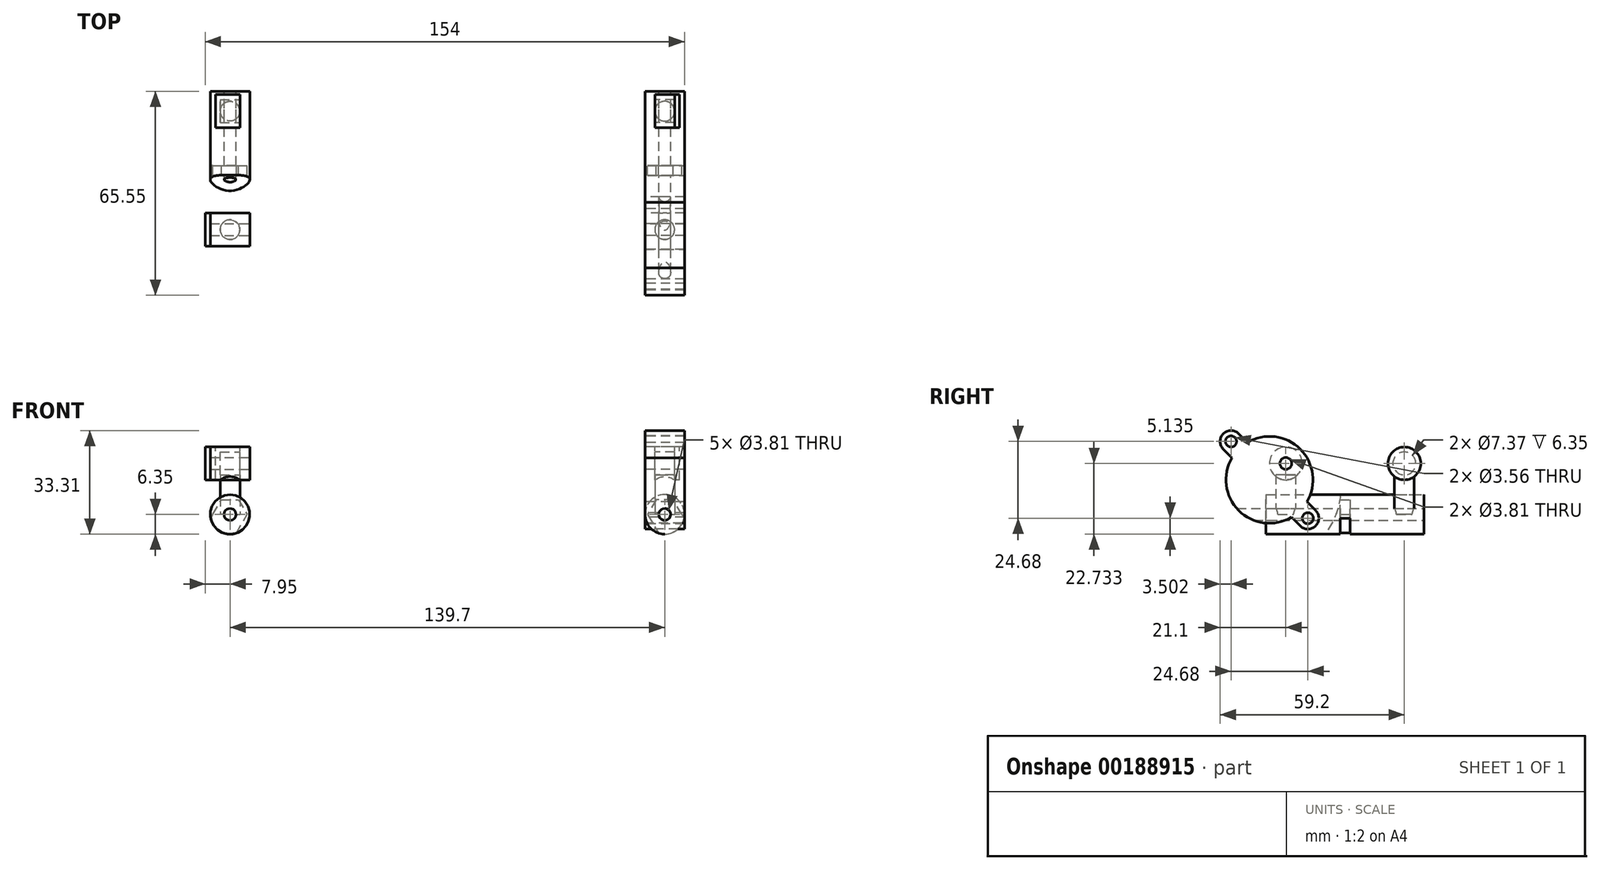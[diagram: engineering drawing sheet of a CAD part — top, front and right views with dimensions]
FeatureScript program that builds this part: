
annotation { "Feature Type Name" : "Feature", "Feature Type Description" : "" }
export const myFeature = defineFeature(function(context is Context, id is Id, definition is map)
    precondition{}
    {
        {
            var Q0;
            Q0=qCreatedBy(makeId("Front.planeOp"),FACE);
            var sketch = newSketch(context, id + "F0", { "sketchPlane" : qUnion([Q0])});
            skCircle(sketch, "E0", {"center": v(-69.85, 0) * mm, "radius": 1.9 * mm});
            skCircle(sketch, "E1", {"center": v(69.85, 0) * mm, "radius": 1.9 * mm});
            skLineSegment(sketch, "E2", {"start": v(-69.85, 0) * mm, "end": v(0, 0) * mm, "construction": true});
            skLineSegment(sketch, "E3", {"start": v(69.85, 0) * mm, "end": v(0, 0) * mm, "construction": true});
            skArc(sketch, "E4", {"start": v(-69.85, 6.35) * mm, "mid": v(-74.34, -4.5) * mm, "end": v(-63.5, 0) * mm});
            skArc(sketch, "E5", {"start": v(63.5, 0) * mm, "mid": v(74.34, -4.5) * mm, "end": v(69.85, 6.35) * mm});
            skLineSegment(sketch, "E6", {"start": v(69.85, 6.35) * mm, "end": v(69.85, 0) * mm, "construction": true});
            skLineSegment(sketch, "E7", {"start": v(-69.85, 6.35) * mm, "end": v(-69.85, 0) * mm, "construction": true});
            skArc(sketch, "E8", {"start": v(-63.5, 0) * mm, "mid": v(-65.36, 4.5) * mm, "end": v(-69.85, 6.35) * mm});
            skArc(sketch, "E9", {"start": v(69.85, 6.35) * mm, "mid": v(65.36, 4.5) * mm, "end": v(63.5, 0) * mm});
            skSolve(sketch);
        }
        {
            var Q0;
            Q0=qSketchRegion(id+"F0",true);
            extrude(context, id + "F1", {"entities" : qUnion([Q0]), "endBound" : BoundingType.SYMMETRIC, "depth" : 12.7 * mm});
        }
        {
            var Q0;
            Q0=makeQuery(id+"F1.opExtrude","CAP_FACE",FACE,{"disambiguationData":[OSD([sQuery(id+"F0.wireOp",EDGE,"E0"),sQuery(id+"F0.wireOp",EDGE,"E1"),sQuery(id+"F0.wireOp",EDGE,"E4"),sQuery(id+"F0.wireOp",EDGE,"E5"),sQuery(id+"F0.wireOp",EDGE,"xyxUVOh0-Lu6m-2nq8-UmFe-XEndblqHEdPT"),sQuery(id+"F0.wireOp",EDGE,"R0XNFQHJ-87U4-ma3Q-qhns-AWXhGPeFOJpI"),sQuery(id+"F0.wireOp",EDGE,"e34iIN8D-vhv8-jKHx-9azW-8f77yfFPg5bW"),sQuery(id+"F0.wireOp",EDGE,"8HNf8llB-7DT9-wTKg-WSqf-SX1znclEPI6e"),sQuery(id+"F0.wireOp",EDGE,"dpBhEA3d-197v-VctA-TAhr-BlY7lmP6uD7G"),sQuery(id+"F0.wireOp",EDGE,"sEkqqTot-DNnZ-R70t-ELHf-v8sBDht2CAfZ")])],"isStart":false});
            var sketch = newSketch(context, id + "F2", { "sketchPlane" : qUnion([Q0])});
            skCircle(sketch, "E10.0", {"center": v(-69.85, 0) * mm, "radius": 1.9 * mm});
            skLineSegment(sketch, "E10.1", {"start": v(-64.48, 3.39) * mm, "end": v(-64.48, 3.39) * mm});
            skLineSegment(sketch, "E11.MirrorCS", {"start": v(64.48, 3.39) * mm, "end": v(64.48, 3.39) * mm});
            skCircle(sketch, "E12.MirrorC", {"center": v(69.85, 0) * mm, "radius": 1.9 * mm});
            skCircle(sketch, "E13.0", {"center": v(69.85, 0) * mm, "radius": 6.35 * mm});
            skCircle(sketch, "E13.1", {"center": v(-69.85, 0) * mm, "radius": 6.35 * mm});
            skSolve(sketch);
        }
        {
            var Q0;
            Q0=qSketchRegion(id+"F2",true);
            extrude(context, id + "F3", {"entities" : qUnion([Q0]), "operationType" : NewBodyOperationType.ADD, "depth" : 19.05 * mm});
        }
        {
            var Q0;
            Q0=makeQuery(id+"F1.opExtrude","SWEPT_BODY",BODY,{"disambiguationData":[OSD([sQuery(id+"F0.wireOp",EDGE,"E0"),sQuery(id+"F0.wireOp",EDGE,"E1"),sQuery(id+"F0.wireOp",EDGE,"E4"),sQuery(id+"F0.wireOp",EDGE,"E5"),sQuery(id+"F0.wireOp",EDGE,"xyxUVOh0-Lu6m-2nq8-UmFe-XEndblqHEdPT"),sQuery(id+"F0.wireOp",EDGE,"R0XNFQHJ-87U4-ma3Q-qhns-AWXhGPeFOJpI"),sQuery(id+"F0.wireOp",EDGE,"e34iIN8D-vhv8-jKHx-9azW-8f77yfFPg5bW"),sQuery(id+"F0.wireOp",EDGE,"8HNf8llB-7DT9-wTKg-WSqf-SX1znclEPI6e"),sQuery(id+"F0.wireOp",EDGE,"dpBhEA3d-197v-VctA-TAhr-BlY7lmP6uD7G"),sQuery(id+"F0.wireOp",EDGE,"sEkqqTot-DNnZ-R70t-ELHf-v8sBDht2CAfZ")])]});
            var Q1;
            Q1=qCreatedBy(makeId("Front.planeOp"),FACE);
            mirror(context, id + "F4", {"operationType" : NewBodyOperationType.ADD, "entities" : qUnion([Q0]), "mirrorPlane" : qUnion([Q1])});
        }
        {
            var Q0;
            Q0=qCreatedBy(makeId("Front.planeOp"),FACE);
            var sketch = newSketch(context, id + "F5", { "sketchPlane" : qUnion([Q0])});
            skCircle(sketch, "E14.cCircle", {"center": v(-69.85, 0) * mm, "radius": 4.76 * mm, "construction": true});
            skLineSegment(sketch, "E14.0", {"start": v(-72.6, 4.76) * mm, "end": v(-67.1, 4.76) * mm});
            skLineSegment(sketch, "E14.1", {"start": v(-67.1, 4.76) * mm, "end": v(-64.35, 0) * mm});
            skLineSegment(sketch, "E14.2", {"start": v(-64.35, 0) * mm, "end": v(-67.1, -4.76) * mm});
            skLineSegment(sketch, "E14.5", {"start": v(-75.35, 0) * mm, "end": v(-72.6, 4.76) * mm});
            skPoint(sketch, "E14.0.midPoint", {"position": v(-69.85, 4.76) * mm});
            skLineSegment(sketch, "E15.MirrorCS", {"start": v(64.35, 0) * mm, "end": v(67.1, -4.76) * mm});
            skLineSegment(sketch, "E16.MirrorCS", {"start": v(75.35, 0) * mm, "end": v(72.6, 4.76) * mm});
            skLineSegment(sketch, "E17.MirrorCS", {"start": v(67.1, 4.76) * mm, "end": v(64.35, 0) * mm});
            skLineSegment(sketch, "E18.MirrorCS", {"start": v(72.6, 4.76) * mm, "end": v(67.1, 4.76) * mm});
            skCircle(sketch, "E19.MirrorC", {"center": v(69.85, 0) * mm, "radius": 4.76 * mm, "construction": true});
            skLineSegment(sketch, "E20", {"start": v(-75.35, 0) * mm, "end": v(-79.15, -6.2) * mm});
            skLineSegment(sketch, "E21", {"start": v(-79.15, -6.2) * mm, "end": v(-70.74, -11.07) * mm});
            skLineSegment(sketch, "E22", {"start": v(-70.74, -11.07) * mm, "end": v(-64.35, 0) * mm});
            skPoint(sketch, "E23.orphan", {"position": v(-72.6, -4.76) * mm});
            skLineSegment(sketch, "E24.MirrorCS", {"start": v(70.74, -11.07) * mm, "end": v(64.35, 0) * mm});
            skLineSegment(sketch, "E25.MirrorCS", {"start": v(75.35, 0) * mm, "end": v(79.15, -6.2) * mm});
            skLineSegment(sketch, "E26.MirrorCS", {"start": v(79.15, -6.2) * mm, "end": v(70.74, -11.07) * mm});
            skPoint(sketch, "E27.orphan", {"position": v(72.6, -4.76) * mm});
            skSolve(sketch);
        }
        {
            var Q0;
            Q0=qSketchRegion(id+"F5",true);
            extrude(context, id + "F6", {"entities" : qUnion([Q0]), "operationType" : NewBodyOperationType.REMOVE, "endBound" : BoundingType.SYMMETRIC, "depth" : 3.17 * mm});
        }
        {
            var Q0;
            Q0=qCreatedBy(makeId("Top.planeOp"),FACE);
            var sketch = newSketch(context, id + "F7", { "sketchPlane" : qUnion([Q0])});
            skCircle(sketch, "E28", {"center": v(-69.85, 19.05) * mm, "radius": 3.18 * mm});
            skCircle(sketch, "E29.MirrorC", {"center": v(69.85, 19.05) * mm, "radius": 3.18 * mm});
            skCircle(sketch, "E30", {"center": v(-69.85, -19.05) * mm, "radius": 3.18 * mm});
            skLineSegment(sketch, "E31", {"start": v(-69.85, 19.05) * mm, "end": v(-69.85, -19.05) * mm, "construction": true});
            skCircle(sketch, "E32.MirrorC", {"center": v(69.85, -19.05) * mm, "radius": 3.18 * mm});
            skSolve(sketch);
        }
        {
            var Q0;
            Q0=qSketchRegion(id+"F7",true);
            extrude(context, id + "F8", {"entities" : qUnion([Q0]), "depth" : 12.7 * mm});
        }
        {
            var Q0;
            Q0=makeQuery(id+"F4.opPattern","COPY",FACE,{"derivedFrom":makeQuery(id+"F3.opExtrude","CAP_FACE",FACE,{"disambiguationData":[OSD([sQuery(id+"F2.wireOp",EDGE,"E10.0"),sQuery(id+"F2.wireOp",EDGE,"E13.1")])],"isStart":false}),"instanceName":"1"});
            var sketch = newSketch(context, id + "F9", { "sketchPlane" : qUnion([Q0])});
            skCircle(sketch, "E33.0", {"center": v(69.85, 0) * mm, "radius": 1.9 * mm});
            skCircle(sketch, "E34.0", {"center": v(-69.85, 0) * mm, "radius": 1.9 * mm});
            skSolve(sketch);
        }
        {
            var Q0;
            Q0=qSketchRegion(id+"F9",true);
            extrude(context, id + "F10", {"entities" : qUnion([Q0]), "operationType" : NewBodyOperationType.REMOVE, "oppositeDirection" : true, "depth" : 42.23 * mm});
        }
        {
            var Q0;
            Q0=qCreatedBy(makeId("Right.planeOp"),FACE);
            cPlane(context, id + "F11", {"entities" : qUnion([Q0]), "cplaneType" : CPlaneType.OFFSET, "offset" : 69.85 * mm, "width" : 152.4 * mm, "height" : 152.4 * mm});
        }
        {
            var Q0;
            Q0=qCreatedBy(id+"F11.planeOp",FACE);
            var sketch = newSketch(context, id + "F12", { "sketchPlane" : qUnion([Q0])});
            skCircle(sketch, "E35", {"center": v(19.05, 16.38) * mm, "radius": 5.28 * mm});
            skCircle(sketch, "E36", {"center": v(19.05, 16.38) * mm, "radius": 3.68 * mm});
            skSolve(sketch);
        }
        {
            var Q0;
            Q0=qSketchRegion(id+"F12",true);
            extrude(context, id + "F13", {"entities" : qUnion([Q0]), "endBound" : BoundingType.SYMMETRIC, "depth" : 6.35 * mm});
        }
        {
            var Q0;
            Q0=makeQuery(id+"F13.opExtrude","SWEPT_BODY",BODY,{"disambiguationData":[OSD([sQuery(id+"F12.wireOp",EDGE,"E35"),sQuery(id+"F12.wireOp",EDGE,"E36")])]});
            var Q1;
            Q1=qCreatedBy(makeId("Right.planeOp"),FACE);
            mirror(context, id + "F14", {"operationType" : NewBodyOperationType.ADD, "entities" : qUnion([Q0]), "mirrorPlane" : qUnion([Q1])});
        }
        {
            var Q0;
            Q0=makeQuery(id+"F13.opExtrude","CAP_FACE",FACE,{"disambiguationData":[OSD([sQuery(id+"F12.wireOp",EDGE,"E35"),sQuery(id+"F12.wireOp",EDGE,"E36")])],"isStart":false});
            var sketch = newSketch(context, id + "F15", { "sketchPlane" : qUnion([Q0])});
            skCircle(sketch, "E37.0", {"center": v(19.05, 16.38) * mm, "radius": 5.28 * mm});
            skSolve(sketch);
        }
        {
            var Q0;
            Q0=qSketchRegion(id+"F15",true);
            extrude(context, id + "F16", {"entities" : qUnion([Q0]), "depth" : 1.52 * mm});
        }
        {
            var Q0;
            Q0=makeQuery(id+"F14.opPattern","COPY",FACE,{"derivedFrom":makeQuery(id+"F13.opExtrude","CAP_FACE",FACE,{"disambiguationData":[OSD([sQuery(id+"F12.wireOp",EDGE,"E35"),sQuery(id+"F12.wireOp",EDGE,"E36")])],"isStart":false}),"instanceName":"1"});
            var sketch = newSketch(context, id + "F17", { "sketchPlane" : qUnion([Q0])});
            skCircle(sketch, "E38.0", {"center": v(-19.05, 16.38) * mm, "radius": 5.28 * mm});
            skSolve(sketch);
        }
        {
            var Q0;
            Q0=qSketchRegion(id+"F17",true);
            extrude(context, id + "F18", {"entities" : qUnion([Q0]), "operationType" : NewBodyOperationType.ADD, "depth" : 1.52 * mm});
        }
        {
            var Q0;
            Q0=qCreatedBy(id+"F11.planeOp",FACE);
            var sketch = newSketch(context, id + "F19", { "sketchPlane" : qUnion([Q0])});
            skCircle(sketch, "E39", {"center": v(-19.05, 16.38) * mm, "radius": 1.9 * mm});
            skLineSegment(sketch, "E40", {"start": v(13.77, 16.38) * mm, "end": v(-19.05, 16.38) * mm, "construction": true});
            skCircle(sketch, "E41.0", {"center": v(19.05, 16.38) * mm, "radius": 5.28 * mm, "construction": true});
            skLineSegment(sketch, "E42", {"start": v(19.05, 16.38) * mm, "end": v(13.77, 16.38) * mm, "construction": true});
            skArc(sketch, "E43", {"start": v(-36.35, 18.21) * mm, "mid": v(-34.19, 1.25) * mm, "end": v(-17.22, -0.91) * mm});
            skArc(sketch, "E44", {"start": v(-34.17, 25.94) * mm, "mid": v(-39.12, 25.94) * mm, "end": v(-39.12, 20.99) * mm});
            skArc(sketch, "E45", {"start": v(-14.44, -3.69) * mm, "mid": v(-9.5, -3.69) * mm, "end": v(-9.5, 1.26) * mm});
            skLineSegment(sketch, "E46", {"start": v(-36.65, 23.46) * mm, "end": v(-24.3, 11.13) * mm, "construction": true});
            skLineSegment(sketch, "E47", {"start": v(-24.3, 11.13) * mm, "end": v(-11.97, -1.21) * mm, "construction": true});
            skLineSegment(sketch, "E48", {"start": v(-19.05, 16.38) * mm, "end": v(-14.43, 21) * mm, "construction": true});
            skLineSegment(sketch, "E49", {"start": v(-36.65, 23.46) * mm, "end": v(-19.05, 16.38) * mm, "construction": true});
            skLineSegment(sketch, "E50", {"start": v(-19.05, 16.38) * mm, "end": v(-11.97, -1.21) * mm, "construction": true});
            skLineSegment(sketch, "E51", {"start": v(-39.12, 20.99) * mm, "end": v(-36.35, 18.21) * mm});
            skLineSegment(sketch, "E52", {"start": v(-34.17, 25.94) * mm, "end": v(-31.4, 23.16) * mm});
            skLineSegment(sketch, "E53", {"start": v(-39.12, 20.99) * mm, "end": v(-36.65, 23.46) * mm, "construction": true});
            skLineSegment(sketch, "E54", {"start": v(-34.17, 25.94) * mm, "end": v(-36.65, 23.46) * mm, "construction": true});
            skLineSegment(sketch, "E55", {"start": v(-14.44, -3.69) * mm, "end": v(-17.22, -0.91) * mm});
            skLineSegment(sketch, "E56", {"start": v(-9.5, 1.26) * mm, "end": v(-12.27, 4.04) * mm});
            skLineSegment(sketch, "E57", {"start": v(-14.44, -3.69) * mm, "end": v(-11.97, -1.21) * mm, "construction": true});
            skLineSegment(sketch, "E58", {"start": v(-11.97, -1.21) * mm, "end": v(-9.5, 1.26) * mm, "construction": true});
            skArc(sketch, "E59.trimOffspring", {"start": v(-12.27, 4.04) * mm, "mid": v(-14.43, 21) * mm, "end": v(-31.4, 23.16) * mm});
            skCircle(sketch, "E60", {"center": v(-36.65, 23.46) * mm, "radius": 1.78 * mm});
            skCircle(sketch, "E61.MirrorC", {"center": v(-11.97, -1.21) * mm, "radius": 1.78 * mm});
            skSolve(sketch);
        }
        {
            var Q0;
            Q0=qSketchRegion(id+"F19",true);
            extrude(context, id + "F20", {"entities" : qUnion([Q0]), "endBound" : BoundingType.SYMMETRIC, "depth" : 12.7 * mm});
        }
        {
            var Q0;
            Q0=makeQuery(id+"F20.opExtrude","SWEPT_BODY",BODY,{"disambiguationData":[OSD([sQuery(id+"F19.wireOp",EDGE,"E39"),sQuery(id+"F19.wireOp",EDGE,"E43"),sQuery(id+"F19.wireOp",EDGE,"E44"),sQuery(id+"F19.wireOp",EDGE,"E45"),sQuery(id+"F19.wireOp",EDGE,"E51"),sQuery(id+"F19.wireOp",EDGE,"E52"),sQuery(id+"F19.wireOp",EDGE,"E55"),sQuery(id+"F19.wireOp",EDGE,"E56"),sQuery(id+"F19.wireOp",EDGE,"E59.trimOffspring")])]});
            var Q1;
            Q1=qCreatedBy(makeId("Right.planeOp"),FACE);
            mirror(context, id + "F21", {"entities" : qUnion([Q0]), "mirrorPlane" : qUnion([Q1])});
        }
        {
            var Q0;
            Q0=makeQuery(id+"F21.opPattern","COPY",FACE,{"derivedFrom":makeQuery(id+"F20.opExtrude","CAP_FACE",FACE,{"disambiguationData":[OSD([sQuery(id+"F19.wireOp",EDGE,"E39"),sQuery(id+"F19.wireOp",EDGE,"E43"),sQuery(id+"F19.wireOp",EDGE,"E44"),sQuery(id+"F19.wireOp",EDGE,"E45"),sQuery(id+"F19.wireOp",EDGE,"E51"),sQuery(id+"F19.wireOp",EDGE,"E52"),sQuery(id+"F19.wireOp",EDGE,"E55"),sQuery(id+"F19.wireOp",EDGE,"E56"),sQuery(id+"F19.wireOp",EDGE,"E59.trimOffspring")])],"isStart":false}),"instanceName":"1"});
            var sketch = newSketch(context, id + "F22", { "sketchPlane" : qUnion([Q0])});
            skCircle(sketch, "E62", {"center": v(19.05, 16.38) * mm, "radius": 5.28 * mm});
            skCircle(sketch, "E63", {"center": v(25.47, 8.62) * mm, "radius": 24.12 * mm});
            skSolve(sketch);
        }
        {
            var Q0;
            Q0=qSketchRegion(id+"F22",true);
            extrude(context, id + "F23", {"entities" : qUnion([Q0]), "operationType" : NewBodyOperationType.REMOVE, "oppositeDirection" : true, "depth" : 25.4 * mm});
        }
        {
            var Q0;
            Q0=makeQuery(id+"F21.opPattern","COPY",FACE,{"derivedFrom":makeQuery(id+"F20.opExtrude","CAP_FACE",FACE,{"disambiguationData":[OSD([sQuery(id+"F19.wireOp",EDGE,"E39"),sQuery(id+"F19.wireOp",EDGE,"E43"),sQuery(id+"F19.wireOp",EDGE,"E44"),sQuery(id+"F19.wireOp",EDGE,"E45"),sQuery(id+"F19.wireOp",EDGE,"E51"),sQuery(id+"F19.wireOp",EDGE,"E52"),sQuery(id+"F19.wireOp",EDGE,"E55"),sQuery(id+"F19.wireOp",EDGE,"E56"),sQuery(id+"F19.wireOp",EDGE,"E59.trimOffspring")])],"isStart":false}),"instanceName":"1"});
            var sketch = newSketch(context, id + "F24", { "sketchPlane" : qUnion([Q0])});
            skCircle(sketch, "E64.0", {"center": v(19.05, 16.38) * mm, "radius": 5.28 * mm});
            skSolve(sketch);
        }
        {
            var Q0;
            Q0=qSketchRegion(id+"F24",true);
            extrude(context, id + "F25", {"entities" : qUnion([Q0]), "depth" : 1.6 * mm});
        }
        {
            var Q0;
            Q0=makeQuery(id+"F4.opPattern","COPY",FACE,{"derivedFrom":makeQuery(id+"F3.opExtrude","CAP_FACE",FACE,{"disambiguationData":[OSD([sQuery(id+"F2.wireOp",EDGE,"E12.MirrorC"),sQuery(id+"F2.wireOp",EDGE,"E13.0")])],"isStart":false}),"instanceName":"1"});
            var sketch = newSketch(context, id + "F26", { "sketchPlane" : qUnion([Q0])});
            skCircle(sketch, "E65.0", {"center": v(-69.85, 0) * mm, "radius": 1.9 * mm});
            skCircle(sketch, "E66.0", {"center": v(69.85, 0) * mm, "radius": 1.9 * mm});
            skSolve(sketch);
        }
        {
            var Q0;
            Q0=qSketchRegion(id+"F26",true);
            extrude(context, id + "F27", {"entities" : qUnion([Q0]), "operationType" : NewBodyOperationType.REMOVE, "oppositeDirection" : true, "depth" : 77.1 * mm});
        }
    });
